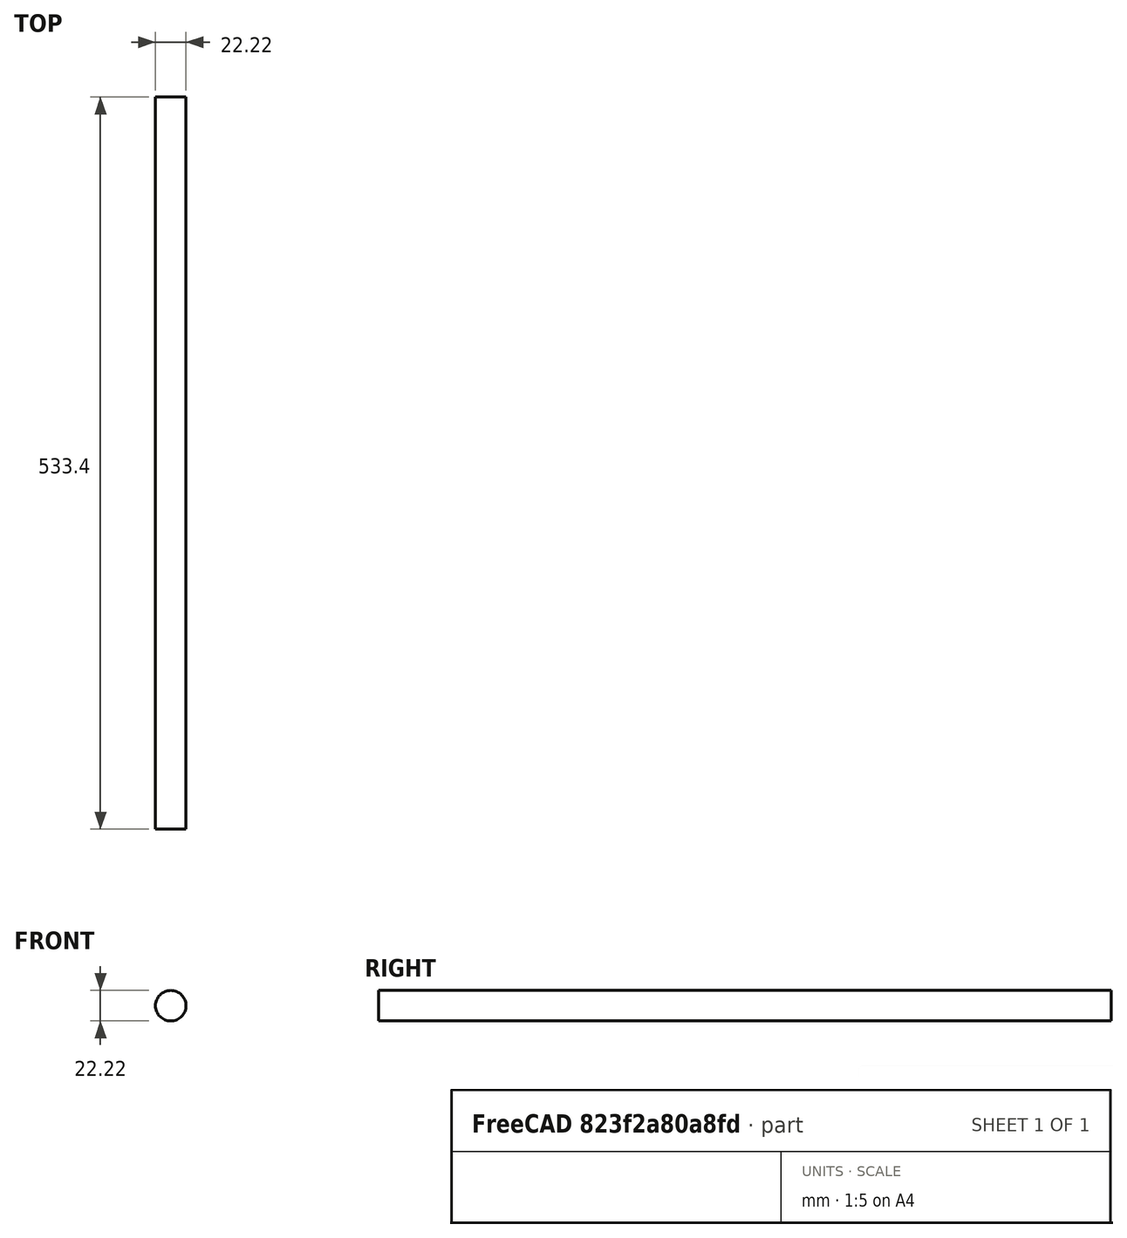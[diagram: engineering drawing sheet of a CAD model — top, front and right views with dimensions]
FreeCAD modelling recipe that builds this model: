
FCSTD DOCUMENT  (FreeCAD 0.20R29603 (Git))
Label: handle
License: All rights reserved
LicenseURL: http://en.wikipedia.org/wiki/All_rights_reserved
objects: TechDraw::DrawProjGroupItem×3, TechDraw::DrawViewDimension×2, Sketcher::SketchObject×1, PartDesign::Pad×1, PartDesign::Body×1, TechDraw::DrawSVGTemplate×1, TechDraw::DrawProjGroup×1, TechDraw::DrawPage×1
note: 4 computed .brp shape members not serialized (recipe doc carries the construction recipe); baked Part::Feature solids carry a one-line shape summary decoded from their .brp

FEATURE [Sketcher::SketchObject] Sketch
  FullyConstrained = true
  MapMode = 5
  Placement = pos=(0,0,0) rot=(1,0,0;1.5708rad)
  Support = -> [XZ_Plane]
  sketch-geometry (1):
    g0: Circle CenterX=0 CenterY=0 CenterZ=0 NormalX=0 NormalY=0 NormalZ=1 AngleXU=0 Radius=11.1125
  constraints (2):
    c: Coincident(g0,g-1)
    c: Diameter(g0) = 22.225
FEATURE [PartDesign::Pad] Pad
  Direction = (0,-1,2e-16)
  Length = 533.4
  Length2 = 10
  Placement = pos=(0,0,0) rot=(1,0,0;1.5708rad)
  Profile = -> Sketch
  ReferenceAxis = -> Sketch [N_Axis]
  Type = 0
FEATURE [PartDesign::Body] Body
  Group = -> [Sketch,Pad]
  Origin = -> Origin
  Tip = -> Pad
FEATURE [TechDraw::DrawSVGTemplate] Template
  Height = 297
  Orientation = 1
  Width = 420
FEATURE [TechDraw::DrawProjGroupItem] ProjItem  label="Front"
  CoarseView = false
  Direction = (-1,0,0)
  Focus = 100
  HardHidden = false
  IsoCount = 0
  IsoHidden = false
  IsoVisible = false
  LockPosition = true
  Perspective = false
  Rotation = 0
  RotationVector = (0,-1,0)
  ScaleType = 2
  SeamHidden = false
  SeamVisible = true
  SmoothHidden = false
  SmoothVisible = true
  Source = -> [Body]
  Type = 0
  X = 0
  XDirection = (0,-1,0)
  Y = 0
FEATURE [TechDraw::DrawProjGroupItem] ProjItem001  label="Left"
  CoarseView = false
  Direction = (-1e-16,1,0)
  Focus = 100
  HardHidden = false
  IsoCount = 0
  IsoHidden = false
  IsoVisible = false
  LockPosition = false
  Perspective = false
  Rotation = 0
  RotationVector = (1,0,0)
  ScaleType = 2
  SeamHidden = false
  SeamVisible = true
  SmoothHidden = false
  SmoothVisible = true
  Source = -> [Body]
  Type = 1
  X = 167.568
  XDirection = (-1,-1e-16,0)
  Y = 0
FEATURE [TechDraw::DrawProjGroupItem] ProjItem002  label="FrontBottomLeft"
  CoarseView = false
  Direction = (-0.57735,0.57735,-0.57735)
  Focus = 100
  HardHidden = false
  IsoCount = 0
  IsoHidden = false
  IsoVisible = false
  LockPosition = false
  Perspective = false
  Rotation = 0
  RotationVector = (1,0,0)
  ScaleType = 2
  SeamHidden = false
  SeamVisible = true
  SmoothHidden = false
  SmoothVisible = true
  Source = -> [Body]
  Type = 8
  X = 143.487
  XDirection = (-0.707107,-0.707107,0)
  Y = 104.269
FEATURE [TechDraw::DrawProjGroup] ProjGroup
  Anchor = -> ProjItem
  AutoDistribute = false
  LockPosition = false
  ProjectionType = 0
  Rotation = 0
  Scale = 0.5
  ScaleType = 0
  Source = -> [Body]
  Views = -> [ProjItem,ProjItem001,ProjItem002]
  X = 154.269
  Y = 109.282
  spacingX = 15.0812
  spacingY = 15.0812
FEATURE [TechDraw::DrawViewDimension] Dimension
  AngleOverride = false
  Arbitrary = false
  ArbitraryTolerances = false
  EqualTolerance = true
  ExtensionAngle = 0
  FormatSpec = ⌀%.2w
  FormatSpecOverTolerance = %+.2w
  FormatSpecUnderTolerance = %+.2w
  Inverted = false
  LineAngle = 0
  LockPosition = false
  MeasureType = 1
  OverTolerance = 0
  References2D = -> [ProjItem001]
  Rotation = 0
  Scale = 0.5
  ScaleType = 0
  TheoreticalExact = false
  Type = 5
  UnderTolerance = 0
  X = 23.9287
  Y = 25.7461
FEATURE [TechDraw::DrawViewDimension] Dimension001
  AngleOverride = false
  Arbitrary = false
  ArbitraryTolerances = false
  EqualTolerance = true
  ExtensionAngle = 0
  FormatSpec = %.2w
  FormatSpecOverTolerance = %+.2w
  FormatSpecUnderTolerance = %+.2w
  Inverted = false
  LineAngle = 0
  LockPosition = false
  MeasureType = 1
  OverTolerance = 0
  References2D = -> [ProjItem]
  Rotation = 0
  Scale = 0.5
  ScaleType = 0
  TheoreticalExact = false
  Type = 1
  UnderTolerance = 0
  X = 2.61701
  Y = 23.838
FEATURE [TechDraw::DrawPage] Page
  KeepUpdated = true
  NextBalloonIndex = 1
  ProjectionType = 0
  Scale = 0.5
  Template = -> Template
  Views = -> [ProjGroup,Dimension,Dimension001]
